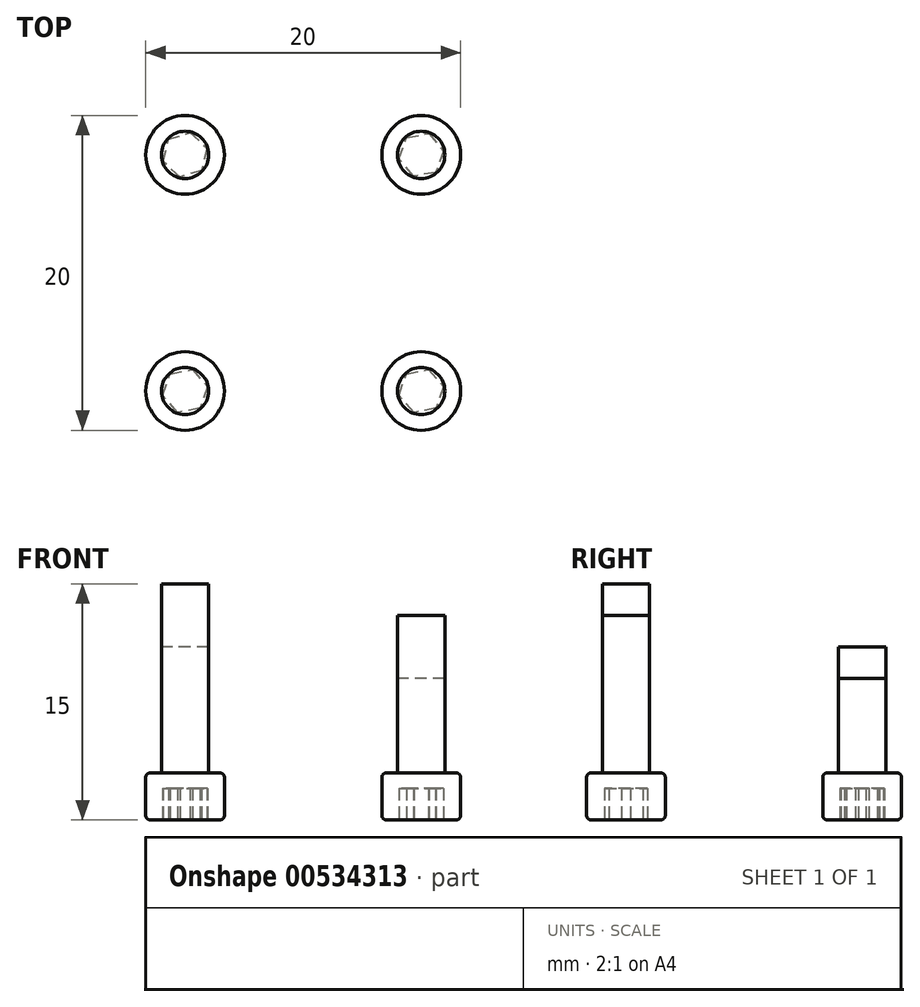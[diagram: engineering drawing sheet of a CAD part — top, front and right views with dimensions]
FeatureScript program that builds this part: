
annotation { "Feature Type Name" : "Feature", "Feature Type Description" : "" }
export const myFeature = defineFeature(function(context is Context, id is Id, definition is map)
    precondition{}
    {
        {
            var Q0;
            Q0=qCreatedBy(makeId("Top.planeOp"),FACE);
            var sketch = newSketch(context, id + "F0", { "sketchPlane" : qUnion([Q0])});
            skLineSegment(sketch, "E0.bottom", {"start": v(7.5, -7.5) * mm, "end": v(-7.5, -7.5) * mm, "construction": true});
            skLineSegment(sketch, "E0.top", {"start": v(7.5, 7.5) * mm, "end": v(-7.5, 7.5) * mm, "construction": true});
            skLineSegment(sketch, "E0.left", {"start": v(7.5, -7.5) * mm, "end": v(7.5, 7.5) * mm, "construction": true});
            skLineSegment(sketch, "E0.right", {"start": v(-7.5, -7.5) * mm, "end": v(-7.5, 7.5) * mm, "construction": true});
            skPoint(sketch, "E0.middle", {"position": v(0, 0) * mm});
            skCircle(sketch, "E1.cCircle", {"center": v(-7.5, 7.5) * mm, "radius": 1.44 * mm, "construction": true});
            skLineSegment(sketch, "E1.0", {"start": v(-6.45, 6.51) * mm, "end": v(-7.83, 6.1) * mm});
            skLineSegment(sketch, "E1.1", {"start": v(-7.83, 6.1) * mm, "end": v(-8.88, 7.08) * mm});
            skLineSegment(sketch, "E1.2", {"start": v(-8.88, 7.08) * mm, "end": v(-8.55, 8.49) * mm});
            skLineSegment(sketch, "E1.3", {"start": v(-8.55, 8.49) * mm, "end": v(-7.17, 8.9) * mm});
            skLineSegment(sketch, "E1.4", {"start": v(-7.17, 8.9) * mm, "end": v(-6.12, 7.92) * mm});
            skLineSegment(sketch, "E1.5", {"start": v(-6.12, 7.92) * mm, "end": v(-6.45, 6.51) * mm});
            skCircle(sketch, "E2.cCircle", {"center": v(7.5, 7.5) * mm, "radius": 1.44 * mm, "construction": true});
            skLineSegment(sketch, "E2.0", {"start": v(8.42, 6.39) * mm, "end": v(7, 6.15) * mm});
            skLineSegment(sketch, "E2.1", {"start": v(7, 6.15) * mm, "end": v(6.08, 7.26) * mm});
            skLineSegment(sketch, "E2.2", {"start": v(6.08, 7.26) * mm, "end": v(6.58, 8.61) * mm});
            skLineSegment(sketch, "E2.3", {"start": v(6.58, 8.61) * mm, "end": v(8, 8.85) * mm});
            skLineSegment(sketch, "E2.4", {"start": v(8, 8.85) * mm, "end": v(8.92, 7.74) * mm});
            skLineSegment(sketch, "E2.5", {"start": v(8.92, 7.74) * mm, "end": v(8.42, 6.39) * mm});
            skCircle(sketch, "E3.cCircle", {"center": v(-7.5, -7.5) * mm, "radius": 1.44 * mm, "construction": true});
            skLineSegment(sketch, "E3.0", {"start": v(-6.55, -8.6) * mm, "end": v(-7.97, -8.86) * mm});
            skLineSegment(sketch, "E3.1", {"start": v(-7.97, -8.86) * mm, "end": v(-8.92, -7.77) * mm});
            skLineSegment(sketch, "E3.2", {"start": v(-8.92, -7.77) * mm, "end": v(-8.45, -6.4) * mm});
            skLineSegment(sketch, "E3.3", {"start": v(-8.45, -6.4) * mm, "end": v(-7.03, -6.14) * mm});
            skLineSegment(sketch, "E3.4", {"start": v(-7.03, -6.14) * mm, "end": v(-6.08, -7.23) * mm});
            skLineSegment(sketch, "E3.5", {"start": v(-6.08, -7.23) * mm, "end": v(-6.55, -8.6) * mm});
            skCircle(sketch, "E4.cCircle", {"center": v(7.5, -7.5) * mm, "radius": 1.44 * mm, "construction": true});
            skLineSegment(sketch, "E4.0", {"start": v(8.45, -8.6) * mm, "end": v(7.03, -8.86) * mm});
            skLineSegment(sketch, "E4.1", {"start": v(7.03, -8.86) * mm, "end": v(6.08, -7.77) * mm});
            skLineSegment(sketch, "E4.2", {"start": v(6.08, -7.77) * mm, "end": v(6.55, -6.4) * mm});
            skLineSegment(sketch, "E4.3", {"start": v(6.55, -6.4) * mm, "end": v(7.97, -6.14) * mm});
            skLineSegment(sketch, "E4.4", {"start": v(7.97, -6.14) * mm, "end": v(8.92, -7.23) * mm});
            skLineSegment(sketch, "E4.5", {"start": v(8.92, -7.23) * mm, "end": v(8.45, -8.6) * mm});
            skCircle(sketch, "E5", {"center": v(-7.5, -7.5) * mm, "radius": 2.5 * mm});
            skCircle(sketch, "E6", {"center": v(7.5, -7.5) * mm, "radius": 2.5 * mm});
            skCircle(sketch, "E7", {"center": v(-7.5, 7.5) * mm, "radius": 2.5 * mm});
            skCircle(sketch, "E8", {"center": v(7.5, 7.5) * mm, "radius": 2.5 * mm});
            skSolve(sketch);
        }
        {
            var Q0;
            Q0=qSketchRegion(id+"F0",true);
            extrude(context, id + "F1", {"entities" : qUnion([Q0]), "depth" : 2 * mm});
        }
        {
            var Q0;
            Q0=qCreatedBy(makeId("Top.planeOp"),FACE);
            cPlane(context, id + "F2", {"entities" : qUnion([Q0]), "cplaneType" : CPlaneType.OFFSET, "offset" : 2 * mm, "width" : 150 * mm, "height" : 150 * mm});
        }
        {
            var Q0;
            Q0=qCreatedBy(id+"F2.planeOp",FACE);
            var sketch = newSketch(context, id + "F3", { "sketchPlane" : qUnion([Q0])});
            skCircle(sketch, "E9.0", {"center": v(-7.5, 7.5) * mm, "radius": 2.5 * mm});
            skCircle(sketch, "E10.0", {"center": v(-7.5, -7.5) * mm, "radius": 2.5 * mm});
            skCircle(sketch, "E11.0", {"center": v(7.5, -7.5) * mm, "radius": 2.5 * mm});
            skCircle(sketch, "E12.0", {"center": v(7.5, 7.5) * mm, "radius": 2.5 * mm});
            skSolve(sketch);
        }
        {
            var Q0;
            Q0=qSketchRegion(id+"F3",true);
            extrude(context, id + "F4", {"entities" : qUnion([Q0]), "operationType" : NewBodyOperationType.ADD, "depth" : 1 * mm});
        }
        {
            var Q0;
            Q0=qCreatedBy(id+"F2.planeOp",FACE);
            cPlane(context, id + "F5", {"entities" : qUnion([Q0]), "cplaneType" : CPlaneType.OFFSET, "offset" : 1 * mm, "width" : 150 * mm, "height" : 150 * mm});
        }
        {
            var Q0;
            Q0=qCreatedBy(id+"F5.planeOp",FACE);
            var sketch = newSketch(context, id + "F6", { "sketchPlane" : qUnion([Q0])});
            skPoint(sketch, "E13.0", {"position": v(7.5, 7.5) * mm});
            skCircle(sketch, "E14", {"center": v(7.5, 7.5) * mm, "radius": 1.5 * mm});
            skPoint(sketch, "E15.0", {"position": v(7.5, -7.5) * mm});
            skCircle(sketch, "E16", {"center": v(7.5, -7.5) * mm, "radius": 1.5 * mm});
            skPoint(sketch, "E17.0", {"position": v(-7.5, -7.5) * mm});
            skCircle(sketch, "E18", {"center": v(-7.5, -7.5) * mm, "radius": 1.5 * mm});
            skPoint(sketch, "E19.0", {"position": v(-7.5, 7.5) * mm});
            skCircle(sketch, "E20", {"center": v(-7.5, 7.5) * mm, "radius": 1.5 * mm});
            skSolve(sketch);
        }
        {
            var Q0;
            Q0=makeQuery(id+"F6.imprint","IMPRINT",FACE,{"disambiguationData":[TD([[makeQuery(id+"F6.imprint","IMPRINT",EDGE,{"derivedFrom":sQuery(id+"F6.wireOp",EDGE,"E14")}),1.0]])]});
            extrude(context, id + "F7", {"entities" : qUnion([Q0]), "operationType" : NewBodyOperationType.ADD, "depth" : 6 * mm});
        }
        {
            var Q0;
            Q0=makeQuery(id+"F6.imprint","IMPRINT",FACE,{"disambiguationData":[TD([[makeQuery(id+"F6.imprint","IMPRINT",EDGE,{"derivedFrom":sQuery(id+"F6.wireOp",EDGE,"E20")}),1.0]])]});
            extrude(context, id + "F8", {"entities" : qUnion([Q0]), "operationType" : NewBodyOperationType.ADD, "depth" : 8 * mm});
        }
        {
            var Q0;
            Q0=makeQuery(id+"F6.imprint","IMPRINT",FACE,{"disambiguationData":[TD([[makeQuery(id+"F6.imprint","IMPRINT",EDGE,{"derivedFrom":sQuery(id+"F6.wireOp",EDGE,"E16")}),1.0]])]});
            extrude(context, id + "F9", {"entities" : qUnion([Q0]), "operationType" : NewBodyOperationType.ADD, "depth" : 10 * mm});
        }
        {
            var Q0;
            Q0=makeQuery(id+"F6.imprint","IMPRINT",FACE,{"disambiguationData":[TD([[makeQuery(id+"F6.imprint","IMPRINT",EDGE,{"derivedFrom":sQuery(id+"F6.wireOp",EDGE,"E18")}),1.0]])]});
            extrude(context, id + "F10", {"entities" : qUnion([Q0]), "operationType" : NewBodyOperationType.ADD, "depth" : 12 * mm});
        }
        {
            var Q0;
            Q0=makeQuery(id+"F4.opExtrude","CAP_EDGE",EDGE,{"disambiguationData":[OSD([sQuery(id+"F3.wireOp",EDGE,"E10.0")])],"isStart":false});
            var Q1;
            Q1=makeQuery(id+"F1.opExtrude","CAP_EDGE",EDGE,{"disambiguationData":[OSD([sQuery(id+"F0.wireOp",EDGE,"E5")])],"isStart":true});
            var Q2;
            Q2=makeQuery(id+"F4.opExtrude","CAP_EDGE",EDGE,{"disambiguationData":[OSD([sQuery(id+"F3.wireOp",EDGE,"E9.0")])],"isStart":false});
            var Q3;
            Q3=makeQuery(id+"F1.opExtrude","CAP_EDGE",EDGE,{"disambiguationData":[OSD([sQuery(id+"F0.wireOp",EDGE,"E7")])],"isStart":true});
            var Q4;
            Q4=makeQuery(id+"F4.opExtrude","CAP_EDGE",EDGE,{"disambiguationData":[OSD([sQuery(id+"F3.wireOp",EDGE,"E12.0")])],"isStart":false});
            var Q5;
            Q5=makeQuery(id+"F1.opExtrude","CAP_EDGE",EDGE,{"disambiguationData":[OSD([sQuery(id+"F0.wireOp",EDGE,"E8")])],"isStart":true});
            var Q6;
            Q6=makeQuery(id+"F4.opExtrude","CAP_EDGE",EDGE,{"disambiguationData":[OSD([sQuery(id+"F3.wireOp",EDGE,"E11.0")])],"isStart":false});
            var Q7;
            Q7=makeQuery(id+"F1.opExtrude","CAP_EDGE",EDGE,{"disambiguationData":[OSD([sQuery(id+"F0.wireOp",EDGE,"E6")])],"isStart":true});
            fillet(context, id + "F11", {"entities" : qUnion([Q0, Q1, Q2, Q3, Q4, Q5, Q6, Q7]), "radius" : 0.3 * mm, "tangentPropagation" : true, "allowEdgeOverflow" : false});
        }
    });
